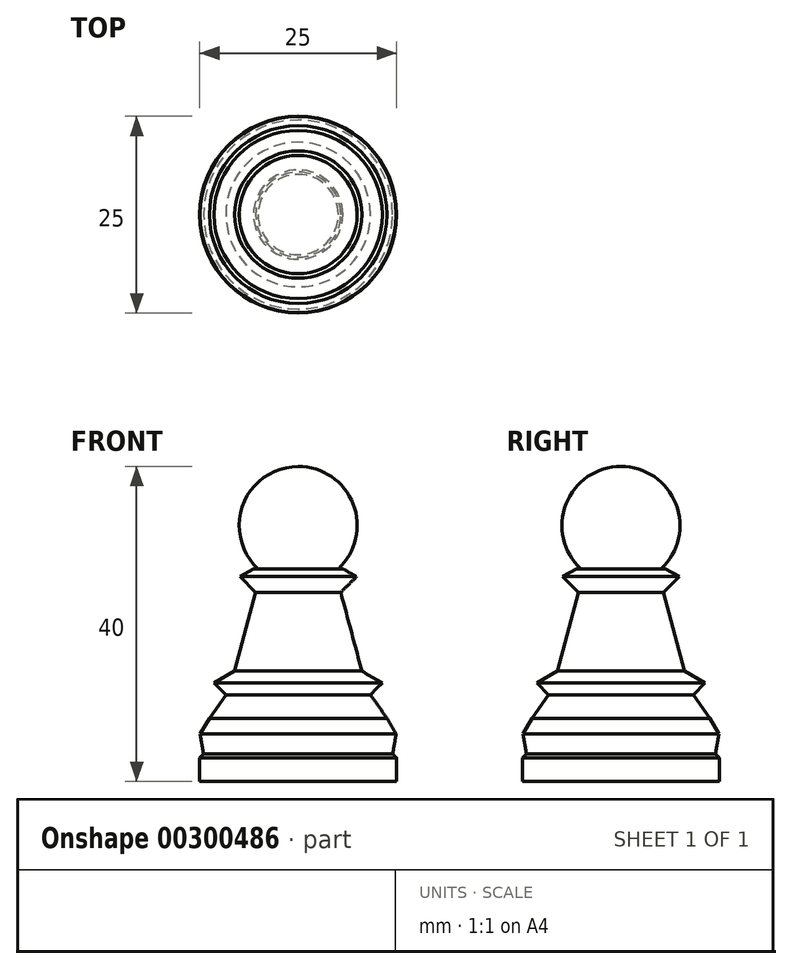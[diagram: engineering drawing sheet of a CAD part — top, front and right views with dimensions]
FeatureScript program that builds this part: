
annotation { "Feature Type Name" : "Feature", "Feature Type Description" : "" }
export const myFeature = defineFeature(function(context is Context, id is Id, definition is map)
    precondition{}
    {
        {
            var Q0;
            Q0=qCreatedBy(makeId("Top.planeOp"),FACE);
            var sketch = newSketch(context, id + "F0", { "sketchPlane" : qUnion([Q0])});
            skCircle(sketch, "E0", {"center": v(0, 0) * mm, "radius": 12.5 * mm});
            skSolve(sketch);
        }
        {
            var Q0;
            Q0=makeQuery(id+"F0.imprint","IMPRINT",FACE,{"disambiguationData":[TD([[makeQuery(id+"F0.imprint","IMPRINT",EDGE,{"derivedFrom":sQuery(id+"F0.wireOp",EDGE,"E0")}),1.0]])]});
            var Q1;
            Q1=sQuery(id+"F0.wireOp",EDGE,"E0");
            extrude(context, id + "F1", {"entities" : qUnion([Q0]), "surfaceEntities" : qUnion([Q1]), "depth" : 3 * mm});
        }
        {
            var Q0;
            Q0=makeQuery(id+"F1.opExtrude","CAP_FACE",FACE,{"disambiguationData":[OSD([sQuery(id+"F0.wireOp",EDGE,"E0")])],"isStart":false});
            extrude(context, id + "F2", {"entities" : qUnion([Q0]), "operationType" : NewBodyOperationType.ADD, "depth" : .5 * mm, "hasDraft" : true, "draftAngle" : 45 * degree, "draftPullDirection" : true});
        }
        {
            var Q0;
            Q0=makeQuery(id+"F2.opExtrude","CAP_FACE",FACE,{"disambiguationData":[OSD([sQuery(id+"F0.wireOp",EDGE,"E0")])],"isStart":false});
            extrude(context, id + "F3", {"entities" : qUnion([Q0]), "operationType" : NewBodyOperationType.ADD, "depth" : 2.5 * mm, "hasDraft" : true, "draftAngle" : 10 * degree});
        }
        {
            var Q0;
            Q0=makeQuery(id+"F3.opExtrude","CAP_FACE",FACE,{"disambiguationData":[OSD([sQuery(id+"F0.wireOp",EDGE,"E0")])],"isStart":false});
            extrude(context, id + "F4", {"entities" : qUnion([Q0]), "operationType" : NewBodyOperationType.ADD, "depth" : 2 * mm, "hasDraft" : true, "draftAngle" : 30 * degree, "draftPullDirection" : true});
        }
        {
            var Q0;
            Q0=makeQuery(id+"F4.opExtrude","CAP_FACE",FACE,{"disambiguationData":[OSD([sQuery(id+"F0.wireOp",EDGE,"E0")])],"isStart":false});
            extrude(context, id + "F5", {"entities" : qUnion([Q0]), "operationType" : NewBodyOperationType.ADD, "depth" : 3 * mm, "hasDraft" : true, "draftAngle" : 35 * degree, "draftPullDirection" : true});
        }
        {
            var Q0;
            Q0=makeQuery(id+"F5.opExtrude","CAP_FACE",FACE,{"disambiguationData":[OSD([sQuery(id+"F0.wireOp",EDGE,"E0")])],"isStart":false});
            extrude(context, id + "F6", {"entities" : qUnion([Q0]), "operationType" : NewBodyOperationType.ADD, "depth" : 1.5 * mm, "hasDraft" : true, "draftAngle" : 45 * degree});
        }
        {
            var Q0;
            Q0=makeQuery(id+"F6.opExtrude","CAP_FACE",FACE,{"disambiguationData":[OSD([sQuery(id+"F0.wireOp",EDGE,"E0")])],"isStart":false});
            extrude(context, id + "F7", {"entities" : qUnion([Q0]), "operationType" : NewBodyOperationType.ADD, "depth" : 1.5 * mm, "hasDraft" : true, "draftAngle" : 60 * degree, "draftPullDirection" : true});
        }
        {
            var Q0;
            Q0=makeQuery(id+"F7.opExtrude","CAP_FACE",FACE,{"disambiguationData":[OSD([sQuery(id+"F0.wireOp",EDGE,"E0")])],"isStart":false});
            extrude(context, id + "F8", {"entities" : qUnion([Q0]), "operationType" : NewBodyOperationType.ADD, "depth" : 10 * mm, "hasDraft" : true, "draftAngle" : 15 * degree, "draftPullDirection" : true});
        }
        {
            var Q0;
            Q0=makeQuery(id+"F8.opExtrude","CAP_FACE",FACE,{"disambiguationData":[OSD([sQuery(id+"F0.wireOp",EDGE,"E0")])],"isStart":false});
            extrude(context, id + "F9", {"entities" : qUnion([Q0]), "operationType" : NewBodyOperationType.ADD, "depth" : 2 * mm, "hasDraft" : true, "draftAngle" : 45 * degree});
        }
        {
            var Q0;
            Q0=makeQuery(id+"F9.opExtrude","CAP_FACE",FACE,{"disambiguationData":[OSD([sQuery(id+"F0.wireOp",EDGE,"E0")])],"isStart":false});
            extrude(context, id + "F10", {"entities" : qUnion([Q0]), "operationType" : NewBodyOperationType.ADD, "depth" : 1 * mm, "hasDraft" : true, "draftAngle" : 60 * degree, "draftPullDirection" : true});
        }
        {
            var Q0;
            Q0=qCreatedBy(makeId("Front.planeOp"),FACE);
            var sketch = newSketch(context, id + "F11", { "sketchPlane" : qUnion([Q0])});
            skLineSegment(sketch, "E1", {"start": v(0, 0) * mm, "end": v(0, 49.73) * mm});
            skCircle(sketch, "E2", {"center": v(0, 32.5) * mm, "radius": 7.5 * mm});
            skSolve(sketch);
        }
        {
            var Q0;
            {var subQ0=sQuery(id+"F11.wireOp",EDGE,"E2");var subQ1=sQuery(id+"F11.wireOp",EDGE,"E1");var subQ2=makeQuery(id+"F11.imprint","INTERSECT",VERTEX,{"disambiguationData":[OD(0.0)],"derivedFrom":[subQ1,subQ0]});Q0=makeQuery(id+"F11.imprint","IMPRINT",FACE,{"disambiguationData":[TD([[makeQuery(id+"F11.imprint","IMPRINT",EDGE,{"disambiguationData":[TD([[subQ2,-1.0]])],"derivedFrom":subQ1}),-1.0]])]});}
            var Q1;
            Q1=sQuery(id+"F11.wireOp",EDGE,"E1");
            revolve(context, id + "F12", {"operationType" : NewBodyOperationType.ADD, "entities" : qUnion([Q0]), "axis" : qUnion([Q1]), "revolveType" : RevolveType.FULL});
        }
    });
